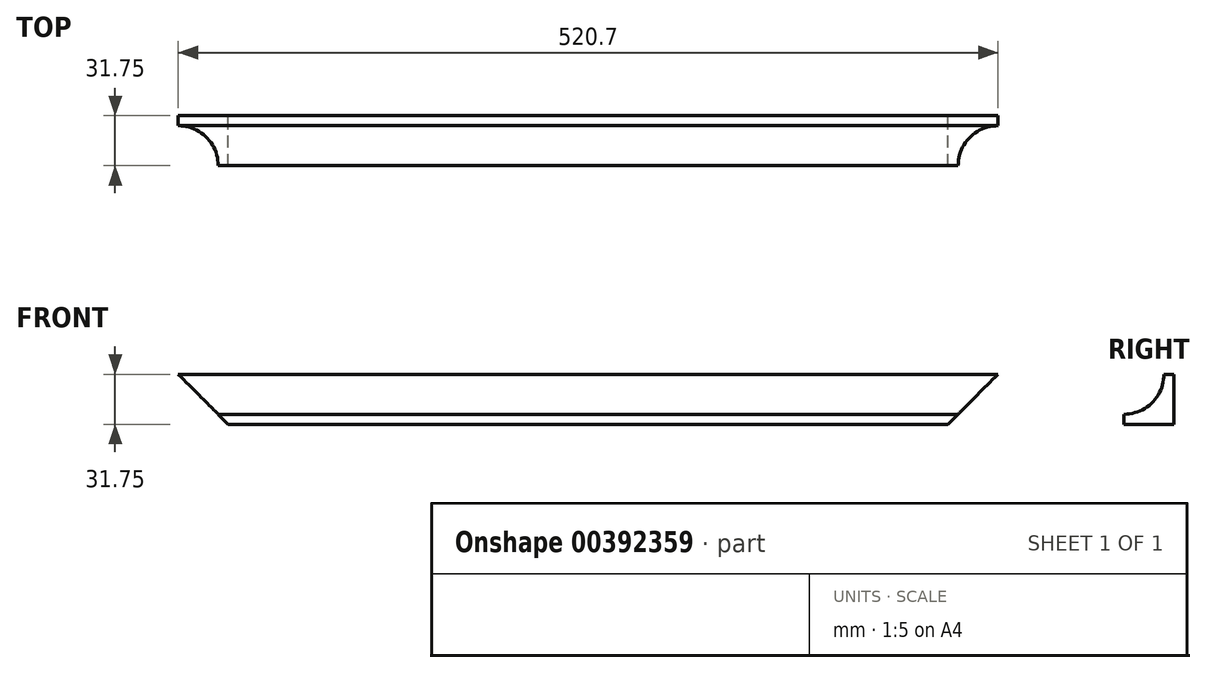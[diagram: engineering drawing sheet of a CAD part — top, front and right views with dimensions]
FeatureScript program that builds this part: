
annotation { "Feature Type Name" : "Feature", "Feature Type Description" : "" }
export const myFeature = defineFeature(function(context is Context, id is Id, definition is map)
    precondition{}
    {
        {
            var Q0;
            Q0=qCreatedBy(makeId("Right.planeOp"),FACE);
            var sketch = newSketch(context, id + "F0", { "sketchPlane" : qUnion([Q0])});
            skLineSegment(sketch, "E0.bottom", {"start": v(0, 0) * mm, "end": v(-31.75, 0) * mm});
            skLineSegment(sketch, "E0.top", {"start": v(0, 31.75) * mm, "end": v(-31.75, 31.75) * mm});
            skLineSegment(sketch, "E0.left", {"start": v(0, 0) * mm, "end": v(0, 31.75) * mm});
            skLineSegment(sketch, "E0.right", {"start": v(-31.75, 0) * mm, "end": v(-31.75, 31.75) * mm});
            skArc(sketch, "E1", {"start": v(-31.75, 6.35) * mm, "mid": v(-13.79, 13.79) * mm, "end": v(-6.35, 31.75) * mm});
            skSolve(sketch);
        }
        {
            var Q0;
            {var subQ1=sQuery(id+"F0.wireOp",EDGE,"E0.bottom");Q0=makeQuery(id+"F0.imprint","IMPRINT",FACE,{"disambiguationData":[TD([[makeQuery(id+"F0.imprint","IMPRINT",EDGE,{"derivedFrom":subQ1}),-1.0]])]});}
            extrude(context, id + "F1", {"entities" : qUnion([Q0]), "depth" : 520.7 * mm});
        }
        {
            var Q0;
            Q0=makeQuery(id+"F1.opExtrude","SWEPT_FACE",FACE,{"disambiguationData":[OSD([sQuery(id+"F0.wireOp",EDGE,"E0.left")])]});
            var sketch = newSketch(context, id + "F2", { "sketchPlane" : qUnion([Q0])});
            skLineSegment(sketch, "E2", {"start": v(-520.7, 31.75) * mm, "end": v(-488.95, 0) * mm});
            skLineSegment(sketch, "E3", {"start": v(0, 31.75) * mm, "end": v(-31.75, 0) * mm});
            skSolve(sketch);
        }
        {
            var Q0;
            {var subQ0=sQuery(id+"F2.wireOp",EDGE,"E3");Q0=makeQuery(id+"F2.imprint","IMPRINT",FACE,{"disambiguationData":[TD([[makeQuery(id+"F2.imprint","IMPRINT",EDGE,{"derivedFrom":subQ0}),1.0]])]});}
            var Q1;
            {var subQ0=sQuery(id+"F2.wireOp",EDGE,"E2");Q1=makeQuery(id+"F2.imprint","IMPRINT",FACE,{"disambiguationData":[TD([[makeQuery(id+"F2.imprint","IMPRINT",EDGE,{"derivedFrom":subQ0}),-1.0]])]});}
            extrude(context, id + "F3", {"entities" : qUnion([Q0, Q1]), "operationType" : NewBodyOperationType.REMOVE, "oppositeDirection" : true, "depth" : 50.8 * mm});
        }
    });
